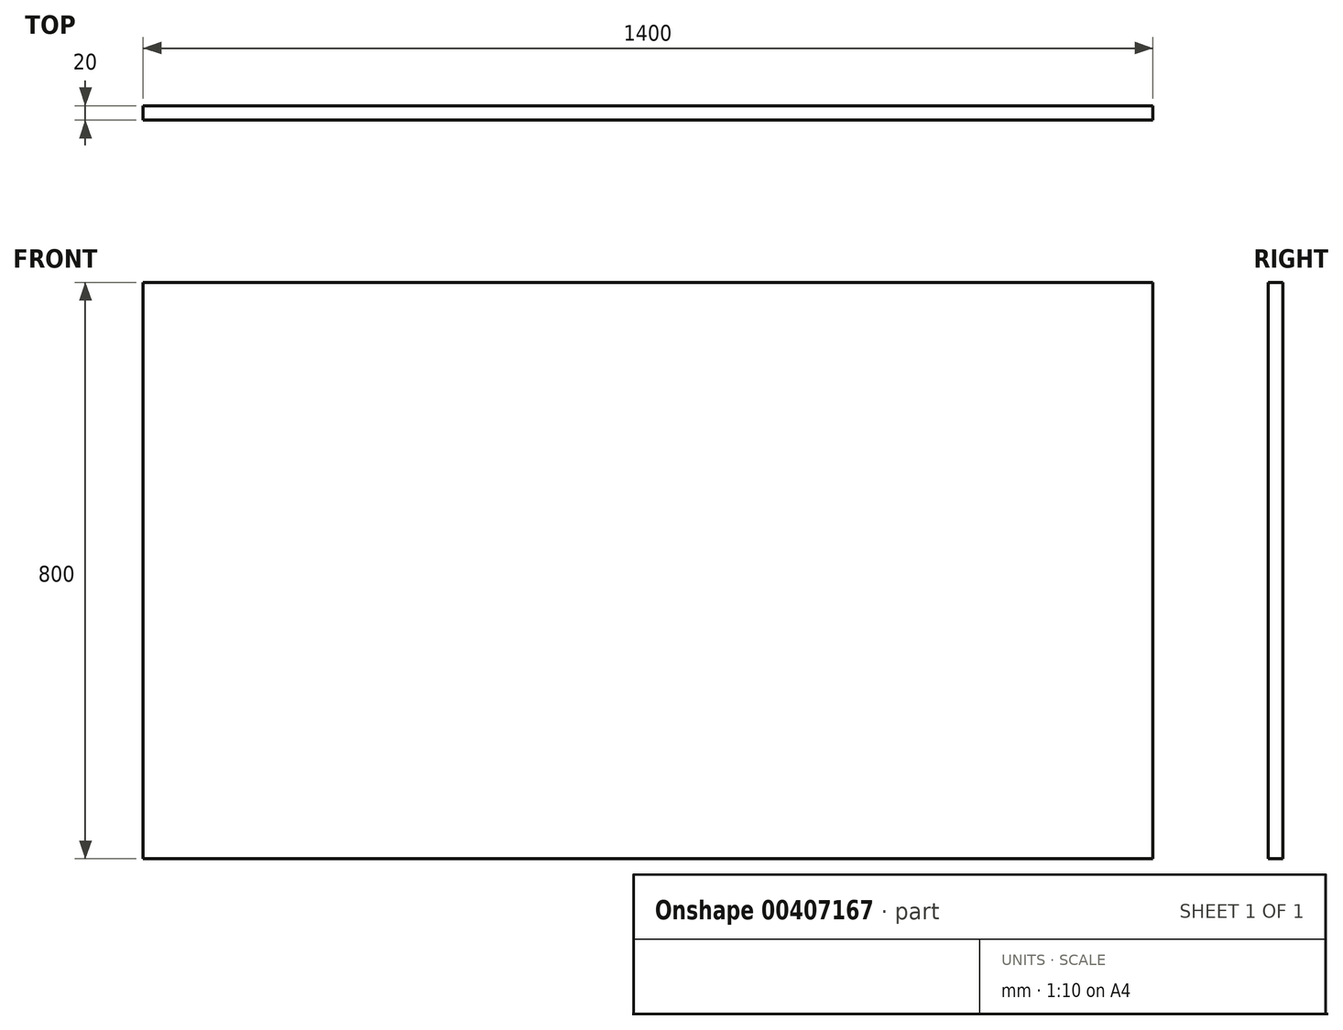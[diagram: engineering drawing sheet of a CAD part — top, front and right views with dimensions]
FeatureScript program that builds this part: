
annotation { "Feature Type Name" : "Feature", "Feature Type Description" : "" }
export const myFeature = defineFeature(function(context is Context, id is Id, definition is map)
    precondition{}
    {
        {
            var Q0;
            Q0=qCreatedBy(makeId("Front.planeOp"),FACE);
            var sketch = newSketch(context, id + "F0", { "sketchPlane" : qUnion([Q0])});
            skLineSegment(sketch, "E0.bottom", {"start": v(-763.86, -275.03) * mm, "end": v(636.14, -275.03) * mm});
            skLineSegment(sketch, "E0.top", {"start": v(-763.86, 524.97) * mm, "end": v(636.14, 524.97) * mm});
            skLineSegment(sketch, "E0.left", {"start": v(-763.86, -275.03) * mm, "end": v(-763.86, 524.97) * mm});
            skLineSegment(sketch, "E0.right", {"start": v(636.14, -275.03) * mm, "end": v(636.14, 524.97) * mm});
            skSolve(sketch);
        }
        {
            var Q0;
            Q0 = qSketchRegion(id + "F0", true);
            extrude(context, id + "F1", {"entities" : qUnion([Q0]), "depth" : 20 * mm});
        }
    });
